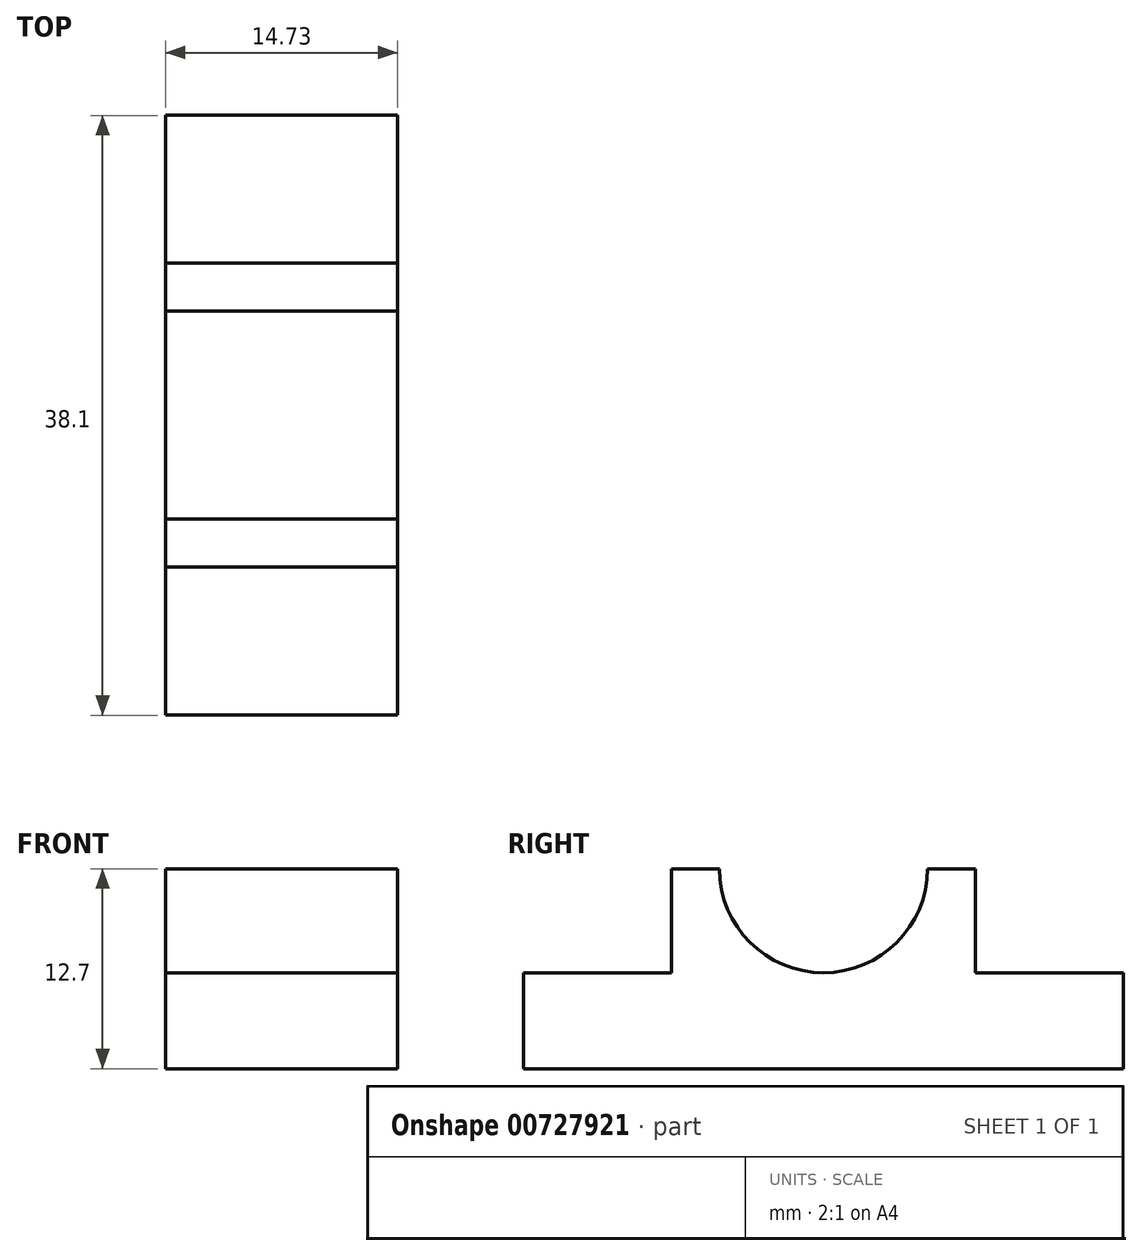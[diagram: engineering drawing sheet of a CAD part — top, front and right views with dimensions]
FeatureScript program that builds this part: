
annotation { "Feature Type Name" : "Feature", "Feature Type Description" : "" }
export const myFeature = defineFeature(function(context is Context, id is Id, definition is map)
    precondition{}
    {
        {
            var Q0;
            Q0=qCreatedBy(makeId("Right.planeOp"),FACE);
            var sketch = newSketch(context, id + "F0", { "sketchPlane" : qUnion([Q0])});
            skLineSegment(sketch, "E0", {"start": v(-76.15, -76.04) * mm, "end": v(-38.05, -76.04) * mm});
            skLineSegment(sketch, "E1", {"start": v(-76.15, -76.04) * mm, "end": v(-76.15, -69.95) * mm});
            skLineSegment(sketch, "E2", {"start": v(-76.15, -69.95) * mm, "end": v(-66.75, -69.95) * mm});
            skLineSegment(sketch, "E3", {"start": v(-66.75, -69.95) * mm, "end": v(-66.75, -63.34) * mm});
            skLineSegment(sketch, "E4", {"start": v(-66.75, -63.34) * mm, "end": v(-47.45, -63.34) * mm});
            skLineSegment(sketch, "E5", {"start": v(-47.45, -63.34) * mm, "end": v(-47.45, -69.95) * mm});
            skLineSegment(sketch, "E6", {"start": v(-47.45, -69.95) * mm, "end": v(-38.05, -69.95) * mm});
            skLineSegment(sketch, "E7", {"start": v(-38.05, -69.95) * mm, "end": v(-38.05, -76.04) * mm});
            skSolve(sketch);
        }
        {
            var Q0;
            Q0=makeQuery(id+"F0.imprint","IMPRINT",FACE,{"disambiguationData":[TD([[makeQuery(id+"F0.imprint","IMPRINT",EDGE,{"derivedFrom":sQuery(id+"F0.wireOp",EDGE,"E0")}),1.0]])]});
            extrude(context, id + "F1", {"entities" : qUnion([Q0]), "depth" : 14.73 * mm, "offsetDistance" : 25.4 * mm});
        }
        {
            var Q0;
            Q0=makeQuery(id+"F1.opExtrude","CAP_FACE",FACE,{"disambiguationData":[OSD([sQuery(id+"F0.wireOp",EDGE,"E0"),sQuery(id+"F0.wireOp",EDGE,"E1"),sQuery(id+"F0.wireOp",EDGE,"E2"),sQuery(id+"F0.wireOp",EDGE,"E3"),sQuery(id+"F0.wireOp",EDGE,"E4"),sQuery(id+"F0.wireOp",EDGE,"E5"),sQuery(id+"F0.wireOp",EDGE,"E6"),sQuery(id+"F0.wireOp",EDGE,"E7")])],"isStart":false});
            var sketch = newSketch(context, id + "F2", { "sketchPlane" : qUnion([Q0])});
            skCircle(sketch, "E8", {"center": v(-57.1, -63.34) * mm, "radius": 6.6 * mm});
            skSolve(sketch);
        }
        {
            var Q0;
            {var subQ0=sQuery(id+"F2.wireOp",EDGE,"E8");var subQ1=makeQuery(id+"F1.opExtrude","CAP_EDGE",EDGE,{"disambiguationData":[OSD([sQuery(id+"F0.wireOp",EDGE,"E4")])],"isStart":false});var subQ2=makeQuery(id+"F2.imprint","INTERSECT",VERTEX,{"disambiguationData":[OD(0.0)],"derivedFrom":[subQ1,subQ0]});Q0=makeQuery(id+"F2.imprint","IMPRINT",FACE,{"disambiguationData":[TD([[makeQuery(id+"F2.imprint","IMPRINT",EDGE,{"disambiguationData":[TD([[subQ2,-1.0]])],"derivedFrom":subQ0}),1.0]])]});}
            extrude(context, id + "F3", {"entities" : qUnion([Q0]), "operationType" : NewBodyOperationType.REMOVE, "endBound" : BoundingType.THROUGH_ALL, "oppositeDirection" : true, "depth" : 25.4 * mm, "offsetDistance" : 25.4 * mm});
        }
    });
